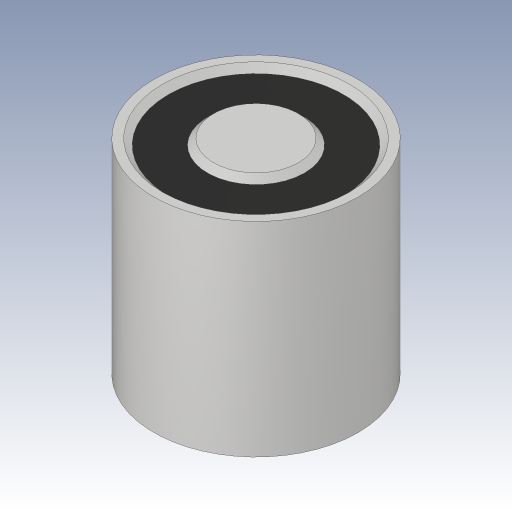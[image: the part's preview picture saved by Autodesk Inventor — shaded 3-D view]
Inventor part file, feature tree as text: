
AUTODESK INVENTOR PART (.ipt)
format: ipt  version: 2023.3 (Build 273359000, 359)  size: 176,640 bytes
history: native  units: in
note: dims shown in document units (in); Inventor stores cm internally (conversion verified against a paired STEP export)
features: sketch x2, revolve x1, chamfer x1, hole x1
ambient origin geometry x8: Origin, YZ Plane, XZ Plane, XY Plane, X Axis, Y Axis, Z Axis, Center Point
bodies: Body1 (feature_tree)
feature tree (5):
  revolve  "Umdrehung1"
  chamfer  "Fase2"  Distance=0.1969in
  hole  "Bohrung1"  [1 undecoded]
  sketch  "Skizze3"  dims[d4=0.2362in]
  sketch  "Skizze4"  dims[d5=0.4724in d6=0.1969in d7=0.1181in d8=0.0138in d9=90.0deg d15=0.0138in d16=0.0197in d17=45.0deg d18=0.0968in d19=0.2362in d20=0.1575in d21=0.0787in d22=90.0deg d23=0.2559in d24=0.0in d10=0.0in d11=0.0in d12=0.0in d13=0.0in]
note: 1 required parameter value undecoded (feature->parameter linkage not recoverable at this tier; creation-order binding heuristic only, values carry confidence <= 0.55)
